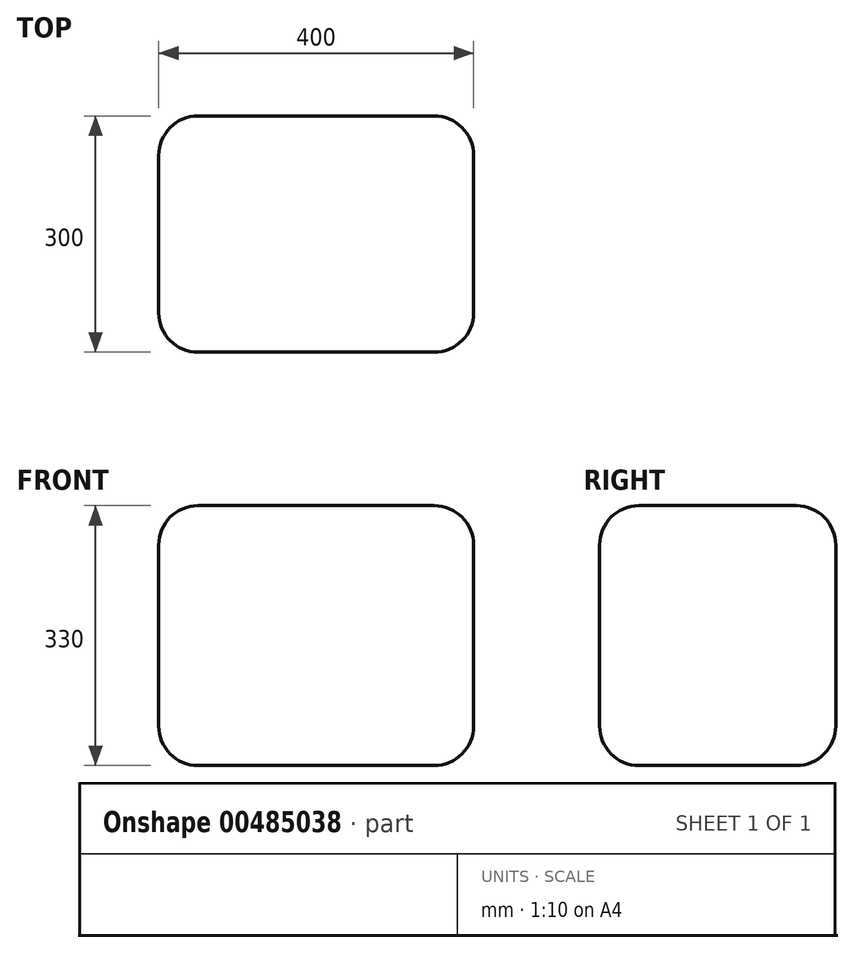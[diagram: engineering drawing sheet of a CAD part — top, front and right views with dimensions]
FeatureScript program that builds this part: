
annotation { "Feature Type Name" : "Feature", "Feature Type Description" : "" }
export const myFeature = defineFeature(function(context is Context, id is Id, definition is map)
    precondition{}
    {
        {
            var Q0;
            Q0=qCreatedBy(makeId("Top.planeOp"),FACE);
            var sketch = newSketch(context, id + "F0", { "sketchPlane" : qUnion([Q0])});
            skLineSegment(sketch, "E0.bottom", {"start": v(200, -150) * mm, "end": v(-200, -150) * mm});
            skLineSegment(sketch, "E0.top", {"start": v(200, 150) * mm, "end": v(-200, 150) * mm});
            skLineSegment(sketch, "E0.left", {"start": v(200, -150) * mm, "end": v(200, 150) * mm});
            skLineSegment(sketch, "E0.right", {"start": v(-200, -150) * mm, "end": v(-200, 150) * mm});
            skPoint(sketch, "E0.middle", {"position": v(0, 0) * mm});
            skSolve(sketch);
        }
        {
            var Q0;
            Q0=makeQuery(id+"F0.imprint","IMPRINT",FACE,{"disambiguationData":[TD([[makeQuery(id+"F0.imprint","IMPRINT",EDGE,{"derivedFrom":sQuery(id+"F0.wireOp",EDGE,"E0.bottom")}),-1.0]])]});
            extrude(context, id + "F1", {"entities" : qUnion([Q0]), "depth" : 330 * mm});
        }
        {
            var Q0;
            Q0=makeQuery(id+"F1.opExtrude","SWEPT_FACE",FACE,{"disambiguationData":[OSD([sQuery(id+"F0.wireOp",EDGE,"E0.top")])]});
            var Q1;
            Q1=makeQuery(id+"F1.opExtrude","CAP_FACE",FACE,{"disambiguationData":[OSD([sQuery(id+"F0.wireOp",EDGE,"E0.bottom"),sQuery(id+"F0.wireOp",EDGE,"E0.top"),sQuery(id+"F0.wireOp",EDGE,"E0.left"),sQuery(id+"F0.wireOp",EDGE,"E0.right")])],"isStart":false});
            var Q2;
            Q2=makeQuery(id+"F1.opExtrude","SWEPT_EDGE",EDGE,{"disambiguationData":[OSD([sQuery(id+"F0.wireOp",EDGE,"E0.top"),sQuery(id+"F0.wireOp",EDGE,"E0.left")])]});
            var Q3;
            Q3=makeQuery(id+"F1.opExtrude","CAP_FACE",FACE,{"disambiguationData":[OSD([sQuery(id+"F0.wireOp",EDGE,"E0.bottom"),sQuery(id+"F0.wireOp",EDGE,"E0.top"),sQuery(id+"F0.wireOp",EDGE,"E0.left"),sQuery(id+"F0.wireOp",EDGE,"E0.right")])],"isStart":true});
            var Q4;
            Q4=makeQuery(id+"F1.opExtrude","SWEPT_EDGE",EDGE,{"disambiguationData":[OSD([sQuery(id+"F0.wireOp",EDGE,"E0.bottom"),sQuery(id+"F0.wireOp",EDGE,"E0.right")])]});
            var Q5;
            Q5=makeQuery(id+"F1.opExtrude","SWEPT_FACE",FACE,{"disambiguationData":[OSD([sQuery(id+"F0.wireOp",EDGE,"E0.bottom")])]});
            var Q6;
            Q6=makeQuery(id+"F1.opExtrude","SWEPT_EDGE",EDGE,{"disambiguationData":[OSD([sQuery(id+"F0.wireOp",EDGE,"E0.bottom"),sQuery(id+"F0.wireOp",EDGE,"E0.left")])]});
            var Q7;
            Q7=makeQuery(id+"F1.opExtrude","CAP_EDGE",EDGE,{"disambiguationData":[OSD([sQuery(id+"F0.wireOp",EDGE,"E0.bottom")])],"isStart":true});
            var Q8;
            Q8=makeQuery(id+"F1.opExtrude","SWEPT_FACE",FACE,{"disambiguationData":[OSD([sQuery(id+"F0.wireOp",EDGE,"E0.left")])]});
            var Q9;
            Q9=makeQuery(id+"F1.opExtrude","CAP_EDGE",EDGE,{"disambiguationData":[OSD([sQuery(id+"F0.wireOp",EDGE,"E0.bottom")])],"isStart":false});
            var Q10;
            Q10=makeQuery(id+"F1.opExtrude","SWEPT_FACE",FACE,{"disambiguationData":[OSD([sQuery(id+"F0.wireOp",EDGE,"E0.right")])]});
            var Q11;
            Q11=makeQuery(id+"F1.opExtrude","CAP_EDGE",EDGE,{"disambiguationData":[OSD([sQuery(id+"F0.wireOp",EDGE,"E0.top")])],"isStart":false});
            var Q12;
            Q12=makeQuery(id+"F1.opExtrude","CAP_EDGE",EDGE,{"disambiguationData":[OSD([sQuery(id+"F0.wireOp",EDGE,"E0.left")])],"isStart":true});
            var Q13;
            Q13=makeQuery(id+"F1.opExtrude","CAP_EDGE",EDGE,{"disambiguationData":[OSD([sQuery(id+"F0.wireOp",EDGE,"E0.left")])],"isStart":false});
            var Q14;
            Q14=makeQuery(id+"F1.opExtrude","CAP_EDGE",EDGE,{"disambiguationData":[OSD([sQuery(id+"F0.wireOp",EDGE,"E0.right")])],"isStart":false});
            var Q15;
            Q15=makeQuery(id+"F1.opExtrude","SWEPT_EDGE",EDGE,{"disambiguationData":[OSD([sQuery(id+"F0.wireOp",EDGE,"E0.top"),sQuery(id+"F0.wireOp",EDGE,"E0.right")])]});
            var Q16;
            Q16=makeQuery(id+"F1.opExtrude","CAP_EDGE",EDGE,{"disambiguationData":[OSD([sQuery(id+"F0.wireOp",EDGE,"E0.top")])],"isStart":true});
            var Q17;
            Q17=makeQuery(id+"F1.opExtrude","CAP_EDGE",EDGE,{"disambiguationData":[OSD([sQuery(id+"F0.wireOp",EDGE,"E0.right")])],"isStart":true});
            fillet(context, id + "F2", {"entities" : qUnion([Q0, Q1, Q2, Q3, Q4, Q5, Q6, Q7, Q8, Q9, Q10, Q11, Q12, Q13, Q14, Q15, Q16, Q17]), "radius" : 50 * mm, "tangentPropagation" : true, "allowEdgeOverflow" : false});
        }
    });
